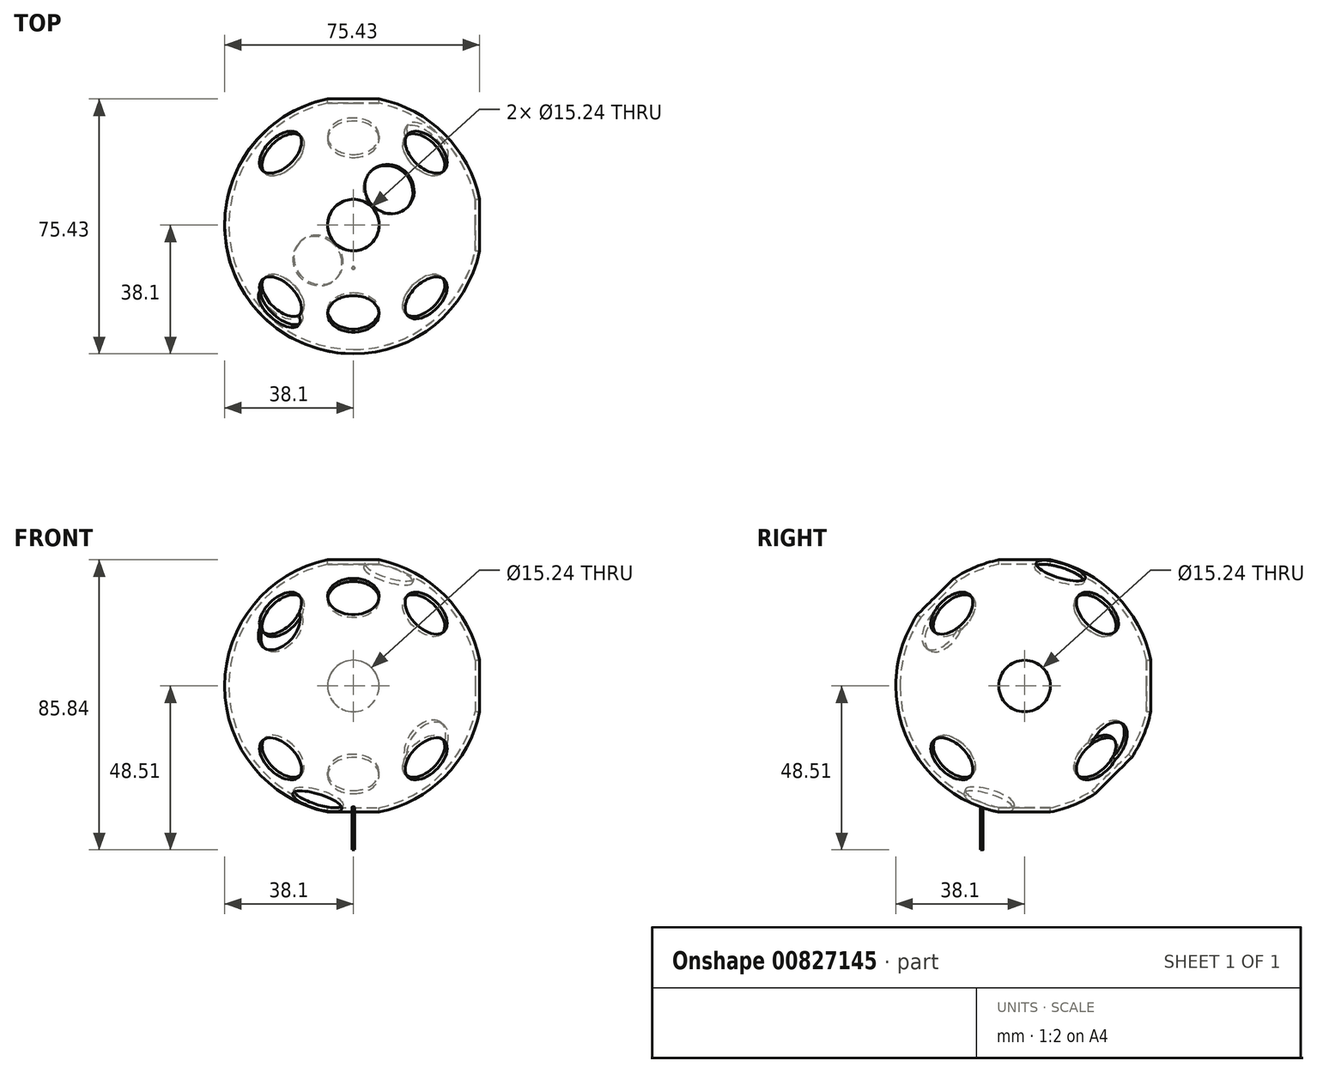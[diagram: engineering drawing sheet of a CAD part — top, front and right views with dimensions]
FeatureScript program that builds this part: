
annotation { "Feature Type Name" : "Feature", "Feature Type Description" : "" }
export const myFeature = defineFeature(function(context is Context, id is Id, definition is map)
    precondition{}
    {
        {
            assignVariable(context, id + "F0", {"name" : "SphereDiameter", "anyValue" : 3});
        }
        {
            var Q0;
            Q0=qCreatedBy(makeId("Top.planeOp"),FACE);
            var sketch = newSketch(context, id + "F1", { "sketchPlane" : qUnion([Q0])});
            skArc(sketch, "E0", {"start": v(0, 38.1) * mm, "mid": v(-38.1, 0) * mm, "end": v(0, -38.1) * mm});
            skLineSegment(sketch, "E1", {"start": v(0, 38.1) * mm, "end": v(0, -38.1) * mm});
            skSolve(sketch);
        }
        {
            var Q0;
            Q0=qSketchRegion(id+"F1",true);
            var Q1;
            Q1=sQuery(id+"F1.wireOp",EDGE,"E1");
            revolve(context, id + "F2", {"surfaceOperationType" : NewSurfaceOperationType.NEW, "entities" : qUnion([Q0]), "axis" : qUnion([Q1]), "revolveType" : RevolveType.FULL});
        }
        {
            var Q0;
            Q0=qCreatedBy(makeId("Top.planeOp"),FACE);
            var sketch = newSketch(context, id + "F3", { "sketchPlane" : qUnion([Q0])});
            skLineSegment(sketch, "E2", {"start": v(0, 0) * mm, "end": v(0, 38.1) * mm});
            skLineSegment(sketch, "E3", {"start": v(0, 0) * mm, "end": v(0, -38.1) * mm});
            skLineSegment(sketch, "E4", {"start": v(0, 0) * mm, "end": v(38.1, 0) * mm});
            skLineSegment(sketch, "E5", {"start": v(0, 0) * mm, "end": v(-38.1, 0) * mm});
            skSolve(sketch);
        }
        {
            var Q0;
            Q0=qCreatedBy(makeId("Front.planeOp"),FACE);
            var sketch = newSketch(context, id + "F4", { "sketchPlane" : qUnion([Q0])});
            skLineSegment(sketch, "E6", {"start": v(0, 0) * mm, "end": v(0, 38.1) * mm});
            skLineSegment(sketch, "E7", {"start": v(0, 0) * mm, "end": v(0, -38.1) * mm});
            skSolve(sketch);
        }
        {
            var Q0;
            Q0=sQuery(id+"F4.wireOp",VERTEX,"E6.end");
            var Q1;
            Q1=sQuery(id+"F3.wireOp",VERTEX,"E3.end");
            var Q2;
            Q2=sQuery(id+"F3.wireOp",VERTEX,"E4.end");
            cPlane(context, id + "F5", {"entities" : qUnion([Q0, Q1, Q2]), "cplaneType" : CPlaneType.THREE_POINT, "offset" : 25.4 * mm, "width" : 152.4 * mm, "height" : 152.4 * mm});
        }
        {
            var Q0;
            Q0=qCreatedBy(id+"F5.planeOp",FACE);
            var sketch = newSketch(context, id + "F6", { "sketchPlane" : qUnion([Q0])});
            skLineSegment(sketch, "E8", {"start": v(-31.1, 0) * mm, "end": v(15.55, -26.94) * mm});
            skLineSegment(sketch, "E9", {"start": v(15.55, -26.94) * mm, "end": v(15.55, 26.94) * mm});
            skLineSegment(sketch, "E10", {"start": v(15.55, 26.94) * mm, "end": v(-31.1, 0) * mm});
            skLineSegment(sketch, "E11", {"start": v(15.55, 26.94) * mm, "end": v(0, 0) * mm});
            skSolve(sketch);
        }
        {
            var Q0;
            Q0=sQuery(id+"F4.wireOp",VERTEX,"E6.end");
            var Q1;
            Q1=sQuery(id+"F6.wireOp",VERTEX,"E11.end");
            var Q2;
            Q2=sQuery(id+"F3.wireOp",VERTEX,"E3.start");
            cPlane(context, id + "F7", {"entities" : qUnion([Q0, Q1, Q2]), "cplaneType" : CPlaneType.THREE_POINT, "offset" : 25.4 * mm, "width" : 152.4 * mm, "height" : 152.4 * mm});
        }
        {
            var Q0;
            Q0=qCreatedBy(id+"F7.planeOp",FACE);
            var sketch = newSketch(context, id + "F8", { "sketchPlane" : qUnion([Q0])});
            skLineSegment(sketch, "E12", {"start": v(0, 0) * mm, "end": v(17.96, 12.7) * mm});
            skLineSegment(sketch, "E13", {"start": v(10.37, 7.33) * mm, "end": v(17.96, 12.7) * mm});
            skLineSegment(sketch, "E14", {"start": v(0, 0) * mm, "end": v(-10.37, -7.33) * mm});
            skSolve(sketch);
        }
        {
            var Q0;
            Q0=sQuery(id+"F3.wireOp",VERTEX,"E2.end");
            var Q1;
            Q1=sQuery(id+"F4.wireOp",VERTEX,"E6.end");
            var Q2;
            Q2=sQuery(id+"F3.wireOp",VERTEX,"E5.end");
            cPlane(context, id + "F9", {"entities" : qUnion([Q0, Q1, Q2]), "cplaneType" : CPlaneType.THREE_POINT, "offset" : 25.4 * mm, "width" : 152.4 * mm, "height" : 152.4 * mm});
        }
        {
            var Q0;
            Q0=qCreatedBy(id+"F9.planeOp",FACE);
            var sketch = newSketch(context, id + "F10", { "sketchPlane" : qUnion([Q0])});
            skLineSegment(sketch, "E15", {"start": v(31.1, 0) * mm, "end": v(-15.55, 26.94) * mm});
            skLineSegment(sketch, "E16", {"start": v(-15.55, 26.94) * mm, "end": v(-15.55, -26.94) * mm});
            skLineSegment(sketch, "E17", {"start": v(-15.55, -26.94) * mm, "end": v(31.1, 0) * mm});
            skLineSegment(sketch, "E18", {"start": v(-15.55, 26.94) * mm, "end": v(0, 0) * mm});
            skSolve(sketch);
        }
        {
            var Q0;
            Q0=sQuery(id+"F4.wireOp",VERTEX,"E6.end");
            var Q1;
            Q1=qCreatedBy(makeId("Origin.pointOp"),VERTEX);
            var Q2;
            Q2=sQuery(id+"F10.wireOp",VERTEX,"E18.end");
            cPlane(context, id + "F11", {"entities" : qUnion([Q0, Q1, Q2]), "cplaneType" : CPlaneType.THREE_POINT, "offset" : 25.4 * mm, "width" : 152.4 * mm, "height" : 152.4 * mm});
        }
        {
            var Q0;
            Q0=qCreatedBy(id+"F11.planeOp",FACE);
            var sketch = newSketch(context, id + "F12", { "sketchPlane" : qUnion([Q0])});
            skLineSegment(sketch, "E19", {"start": v(0, 0) * mm, "end": v(-17.96, 12.7) * mm});
            skLineSegment(sketch, "E20", {"start": v(-17.96, 12.7) * mm, "end": v(-10.37, 7.33) * mm});
            skLineSegment(sketch, "E21", {"start": v(10.37, -7.33) * mm, "end": v(0, 0) * mm});
            skSolve(sketch);
        }
        {
            var Q0;
            Q0=sQuery(id+"F3.wireOp",VERTEX,"E2.end");
            var Q1;
            Q1=sQuery(id+"F4.wireOp",VERTEX,"E7.end");
            var Q2;
            Q2=sQuery(id+"F3.wireOp",VERTEX,"E4.end");
            cPlane(context, id + "F13", {"entities" : qUnion([Q0, Q1, Q2]), "cplaneType" : CPlaneType.THREE_POINT, "offset" : 25.4 * mm, "width" : 152.4 * mm, "height" : 152.4 * mm});
        }
        {
            var Q0;
            Q0=qCreatedBy(id+"F13.planeOp",FACE);
            var sketch = newSketch(context, id + "F14", { "sketchPlane" : qUnion([Q0])});
            skLineSegment(sketch, "E22", {"start": v(15.55, -26.94) * mm, "end": v(15.55, 26.94) * mm});
            skLineSegment(sketch, "E23", {"start": v(15.55, 26.94) * mm, "end": v(-31.1, 0) * mm});
            skLineSegment(sketch, "E24", {"start": v(-31.1, 0) * mm, "end": v(15.55, -26.94) * mm});
            skLineSegment(sketch, "E25", {"start": v(15.55, 26.94) * mm, "end": v(0, 0) * mm});
            skSolve(sketch);
        }
        {
            var Q0;
            Q0=sQuery(id+"F3.wireOp",VERTEX,"E3.start");
            var Q1;
            Q1=sQuery(id+"F3.wireOp",VERTEX,"E2.end");
            var Q2;
            Q2=sQuery(id+"F14.wireOp",VERTEX,"E25.end");
            cPlane(context, id + "F15", {"entities" : qUnion([Q0, Q1, Q2]), "cplaneType" : CPlaneType.THREE_POINT, "offset" : 25.4 * mm, "width" : 152.4 * mm, "height" : 152.4 * mm});
        }
        {
            var Q0;
            Q0=qCreatedBy(id+"F15.planeOp",FACE);
            var sketch = newSketch(context, id + "F16", { "sketchPlane" : qUnion([Q0])});
            skLineSegment(sketch, "E26", {"start": v(0, 0) * mm, "end": v(17.96, 12.7) * mm});
            skLineSegment(sketch, "E27", {"start": v(10.37, 7.33) * mm, "end": v(17.96, 12.7) * mm});
            skLineSegment(sketch, "E28", {"start": v(0, 0) * mm, "end": v(-10.37, -7.33) * mm});
            skSolve(sketch);
        }
        {
            var Q0;
            Q0=sQuery(id+"F4.wireOp",VERTEX,"E6.end");
            var Q1;
            Q1=sQuery(id+"F3.wireOp",VERTEX,"E4.end");
            var Q2;
            Q2=sQuery(id+"F3.wireOp",VERTEX,"E2.end");
            cPlane(context, id + "F17", {"entities" : qUnion([Q0, Q1, Q2]), "cplaneType" : CPlaneType.THREE_POINT, "offset" : 25.4 * mm, "width" : 152.4 * mm, "height" : 152.4 * mm});
        }
        {
            var Q0;
            Q0=qCreatedBy(id+"F17.planeOp",FACE);
            var sketch = newSketch(context, id + "F18", { "sketchPlane" : qUnion([Q0])});
            skLineSegment(sketch, "E29", {"start": v(-15.55, 26.94) * mm, "end": v(31.1, 0) * mm});
            skLineSegment(sketch, "E30", {"start": v(31.1, 0) * mm, "end": v(-15.55, -26.94) * mm});
            skLineSegment(sketch, "E31", {"start": v(-15.55, -26.94) * mm, "end": v(-15.55, 26.94) * mm});
            skLineSegment(sketch, "E32", {"start": v(-15.55, 26.94) * mm, "end": v(0, 0) * mm});
            skSolve(sketch);
        }
        {
            var Q0;
            Q0=sQuery(id+"F4.wireOp",VERTEX,"E6.end");
            var Q1;
            Q1=sQuery(id+"F18.wireOp",VERTEX,"E32.end");
            var Q2;
            Q2=sQuery(id+"F3.wireOp",VERTEX,"E3.start");
            cPlane(context, id + "F19", {"entities" : qUnion([Q0, Q1, Q2]), "cplaneType" : CPlaneType.THREE_POINT, "offset" : 25.4 * mm, "width" : 152.4 * mm, "height" : 152.4 * mm});
        }
        {
            var Q0;
            Q0=qCreatedBy(id+"F19.planeOp",FACE);
            var sketch = newSketch(context, id + "F20", { "sketchPlane" : qUnion([Q0])});
            skLineSegment(sketch, "E33", {"start": v(0, 0) * mm, "end": v(17.96, 12.7) * mm});
            skLineSegment(sketch, "E34", {"start": v(10.37, 7.33) * mm, "end": v(17.96, 12.7) * mm});
            skLineSegment(sketch, "E35", {"start": v(0, 0) * mm, "end": v(-10.37, -7.33) * mm});
            skSolve(sketch);
        }
        {
            var Q0;
            Q0=qCreatedBy(makeId("Top.planeOp"),FACE);
            var Q1;
            Q1=sQuery(id+"F4.wireOp",VERTEX,"E6.end");
            cPlane(context, id + "F21", {"entities" : qUnion([Q0, Q1]), "cplaneType" : CPlaneType.PLANE_POINT, "offset" : 25.4 * mm, "width" : 152.4 * mm, "height" : 152.4 * mm});
        }
        {
            var Q0;
            Q0=qCreatedBy(id+"F21.planeOp",FACE);
            var sketch = newSketch(context, id + "F22", { "sketchPlane" : qUnion([Q0])});
            skCircle(sketch, "E36", {"center": v(0, 0) * mm, "radius": 7.62 * mm});
            skSolve(sketch);
        }
        {
            var Q0;
            Q0=qSketchRegion(id+"F22",true);
            extrude(context, id + "F23", {"entities" : qUnion([Q0]), "operationType" : NewBodyOperationType.REMOVE, "endBound" : BoundingType.SYMMETRIC, "oppositeDirection" : true, "depth" : 76.2 * mm, "offsetDistance" : 25.4 * mm});
        }
        {
            var Q0;
            Q0=qCreatedBy(makeId("Right.planeOp"),FACE);
            var Q1;
            Q1=sQuery(id+"F3.wireOp",VERTEX,"E4.end");
            cPlane(context, id + "F24", {"entities" : qUnion([Q0, Q1]), "cplaneType" : CPlaneType.PLANE_POINT, "offset" : 25.4 * mm, "width" : 152.4 * mm, "height" : 152.4 * mm});
        }
        {
            var Q0;
            Q0=qCreatedBy(id+"F24.planeOp",FACE);
            var sketch = newSketch(context, id + "F25", { "sketchPlane" : qUnion([Q0])});
            skCircle(sketch, "E37", {"center": v(0, 0) * mm, "radius": 7.62 * mm});
            skSolve(sketch);
        }
        {
            var Q0;
            Q0=qSketchRegion(id+"F25",true);
            extrude(context, id + "F26", {"entities" : qUnion([Q0]), "operationType" : NewBodyOperationType.REMOVE, "endBound" : BoundingType.SYMMETRIC, "oppositeDirection" : true, "depth" : 76.2 * mm, "offsetDistance" : 25.4 * mm});
        }
        {
            var Q0;
            Q0=qCreatedBy(makeId("Front.planeOp"),FACE);
            var Q1;
            Q1=sQuery(id+"F3.wireOp",VERTEX,"E2.end");
            cPlane(context, id + "F27", {"entities" : qUnion([Q0, Q1]), "cplaneType" : CPlaneType.PLANE_POINT, "offset" : 25.4 * mm, "width" : 152.4 * mm, "height" : 152.4 * mm});
        }
        {
            var Q0;
            Q0=qCreatedBy(id+"F27.planeOp",FACE);
            var sketch = newSketch(context, id + "F28", { "sketchPlane" : qUnion([Q0])});
            skCircle(sketch, "E38", {"center": v(0, 0) * mm, "radius": 7.62 * mm});
            skSolve(sketch);
        }
        {
            var Q0;
            Q0=qSketchRegion(id+"F28",true);
            extrude(context, id + "F29", {"entities" : qUnion([Q0]), "operationType" : NewBodyOperationType.REMOVE, "endBound" : BoundingType.SYMMETRIC, "depth" : 76.2 * mm, "offsetDistance" : 25.4 * mm});
        }
        {
            var Q0;
            Q0=qCreatedBy(id+"F5.planeOp",FACE);
            var Q1;
            Q1=sQuery(id+"F8.wireOp",VERTEX,"E13.end");
            cPlane(context, id + "F30", {"entities" : qUnion([Q0, Q1]), "cplaneType" : CPlaneType.PLANE_POINT, "offset" : 25.4 * mm, "width" : 152.4 * mm, "height" : 152.4 * mm});
        }
        {
            var Q0;
            Q0=qCreatedBy(id+"F30.planeOp",FACE);
            var sketch = newSketch(context, id + "F31", { "sketchPlane" : qUnion([Q0])});
            skCircle(sketch, "E39", {"center": v(0, 0) * mm, "radius": 7.62 * mm});
            skSolve(sketch);
        }
        {
            var Q0;
            Q0=qSketchRegion(id+"F31",true);
            extrude(context, id + "F32", {"entities" : qUnion([Q0]), "operationType" : NewBodyOperationType.REMOVE, "endBound" : BoundingType.SYMMETRIC, "depth" : 254 * mm, "offsetDistance" : 25.4 * mm});
        }
        {
            var Q0;
            Q0=qCreatedBy(id+"F9.planeOp",FACE);
            var Q1;
            Q1=sQuery(id+"F12.wireOp",VERTEX,"E20.start");
            cPlane(context, id + "F33", {"entities" : qUnion([Q0, Q1]), "cplaneType" : CPlaneType.PLANE_POINT, "offset" : 25.4 * mm, "width" : 152.4 * mm, "height" : 152.4 * mm});
        }
        {
            var Q0;
            Q0=qCreatedBy(id+"F33.planeOp",FACE);
            var sketch = newSketch(context, id + "F34", { "sketchPlane" : qUnion([Q0])});
            skCircle(sketch, "E40", {"center": v(0, 0) * mm, "radius": 7.62 * mm});
            skSolve(sketch);
        }
        {
            var Q0;
            Q0=qSketchRegion(id+"F34",true);
            extrude(context, id + "F35", {"entities" : qUnion([Q0]), "operationType" : NewBodyOperationType.REMOVE, "endBound" : BoundingType.SYMMETRIC, "depth" : 254 * mm, "offsetDistance" : 25.4 * mm});
        }
        {
            var Q0;
            Q0=qCreatedBy(id+"F17.planeOp",FACE);
            var Q1;
            Q1=sQuery(id+"F20.wireOp",VERTEX,"E34.end");
            cPlane(context, id + "F36", {"entities" : qUnion([Q0, Q1]), "cplaneType" : CPlaneType.PLANE_POINT, "offset" : 25.4 * mm, "width" : 152.4 * mm, "height" : 152.4 * mm});
        }
        {
            var Q0;
            Q0=qCreatedBy(id+"F36.planeOp",FACE);
            var sketch = newSketch(context, id + "F37", { "sketchPlane" : qUnion([Q0])});
            skCircle(sketch, "E41", {"center": v(0, 0) * mm, "radius": 7.62 * mm});
            skSolve(sketch);
        }
        {
            var Q0;
            Q0=qSketchRegion(id+"F37",true);
            extrude(context, id + "F38", {"entities" : qUnion([Q0]), "operationType" : NewBodyOperationType.REMOVE, "endBound" : BoundingType.SYMMETRIC, "depth" : 254 * mm, "offsetDistance" : 25.4 * mm});
        }
        {
            var Q0;
            Q0=qCreatedBy(id+"F13.planeOp",FACE);
            var Q1;
            Q1=sQuery(id+"F16.wireOp",VERTEX,"E27.end");
            cPlane(context, id + "F39", {"entities" : qUnion([Q0, Q1]), "cplaneType" : CPlaneType.PLANE_POINT, "offset" : 25.4 * mm, "width" : 152.4 * mm, "height" : 152.4 * mm});
        }
        {
            var Q0;
            Q0=qCreatedBy(id+"F39.planeOp",FACE);
            var sketch = newSketch(context, id + "F40", { "sketchPlane" : qUnion([Q0])});
            skCircle(sketch, "E42", {"center": v(0, 0) * mm, "radius": 7.62 * mm});
            skSolve(sketch);
        }
        {
            var Q0;
            Q0=qSketchRegion(id+"F40",true);
            extrude(context, id + "F41", {"entities" : qUnion([Q0]), "operationType" : NewBodyOperationType.REMOVE, "endBound" : BoundingType.SYMMETRIC, "depth" : 254 * mm, "offsetDistance" : 25.4 * mm});
        }
        {
            var Q0;
            Q0=qCreatedBy(makeId("Top.planeOp"),FACE);
            var sketch = newSketch(context, id + "F42", { "sketchPlane" : qUnion([Q0])});
            skArc(sketch, "E43", {"start": v(0, 36.83) * mm, "mid": v(-36.83, 0) * mm, "end": v(0, -36.83) * mm});
            skLineSegment(sketch, "E44", {"start": v(0, 36.83) * mm, "end": v(0, -36.83) * mm});
            skSolve(sketch);
        }
        {
            var Q0;
            Q0=qSketchRegion(id+"F42",true);
            var Q1;
            Q1=sQuery(id+"F3.wireOp",EDGE,"E2");
            revolve(context, id + "F43", {"operationType" : NewBodyOperationType.REMOVE, "surfaceOperationType" : NewSurfaceOperationType.NEW, "entities" : qUnion([Q0]), "axis" : qUnion([Q1]), "revolveType" : RevolveType.FULL, "oppositeDirection" : true});
        }
        {
            var Q0;
            Q0=sQuery(id+"F12.wireOp",VERTEX,"E20.start");
            var Q1;
            Q1=sQuery(id+"F28.wireOp",VERTEX,"E38.center");
            var Q2;
            Q2=sQuery(id+"F20.wireOp",VERTEX,"E34.end");
            cPlane(context, id + "F44", {"entities" : qUnion([Q0, Q1, Q2]), "cplaneType" : CPlaneType.THREE_POINT, "offset" : 25.4 * mm, "width" : 152.4 * mm, "height" : 152.4 * mm});
        }
        {
            var Q0;
            Q0=qCreatedBy(id+"F44.planeOp",FACE);
            var sketch = newSketch(context, id + "F45", { "sketchPlane" : qUnion([Q0])});
            skLineSegment(sketch, "E45", {"start": v(7.33, 5.43) * mm, "end": v(-7.33, 5.43) * mm});
            skLineSegment(sketch, "E46", {"start": v(0, 37.06) * mm, "end": v(0, 5.43) * mm});
            skSolve(sketch);
        }
        {
            var Q0;
            Q0=sQuery(id+"F4.wireOp",VERTEX,"E6.end");
            var Q1;
            Q1=sQuery(id+"F20.wireOp",VERTEX,"E34.end");
            var Q2;
            Q2=sQuery(id+"F12.wireOp",VERTEX,"E20.start");
            cPlane(context, id + "F46", {"entities" : qUnion([Q0, Q1, Q2]), "cplaneType" : CPlaneType.THREE_POINT, "offset" : 25.4 * mm, "width" : 152.4 * mm, "height" : 152.4 * mm});
        }
        {
            var Q0;
            Q0=qCreatedBy(id+"F46.planeOp",FACE);
            var sketch = newSketch(context, id + "F47", { "sketchPlane" : qUnion([Q0])});
            skLineSegment(sketch, "E47", {"start": v(0, 37.06) * mm, "end": v(0, 5.43) * mm});
            skSolve(sketch);
        }
        {
            var Q0;
            Q0=qCreatedBy(id+"F46.planeOp",FACE);
            var sketch = newSketch(context, id + "F48", { "sketchPlane" : qUnion([Q0])});
            skLineSegment(sketch, "E48", {"start": v(0, -2.1) * mm, "end": v(0, 5.43) * mm});
            skSolve(sketch);
        }
        {
            var Q0;
            Q0=qCreatedBy(id+"F44.planeOp",FACE);
            var sketch = newSketch(context, id + "F49", { "sketchPlane" : qUnion([Q0])});
            skLineSegment(sketch, "E49", {"start": v(0, 5.43) * mm, "end": v(0, -2.1) * mm});
            skSolve(sketch);
        }
        {
            var Q0;
            Q0=sQuery(id+"F12.wireOp",VERTEX,"E19.start");
            var Q1;
            Q1=sQuery(id+"F12.wireOp",VERTEX,"E20.start");
            var Q2;
            Q2=sQuery(id+"F20.wireOp",VERTEX,"E34.end");
            cPlane(context, id + "F50", {"entities" : qUnion([Q0, Q1, Q2]), "cplaneType" : CPlaneType.THREE_POINT, "offset" : 25.4 * mm, "width" : 152.4 * mm, "height" : 152.4 * mm});
        }
        {
            var Q0;
            Q0=sQuery(id+"F49.wireOp",VERTEX,"E49.start");
            var Q1;
            Q1=sQuery(id+"F48.wireOp",VERTEX,"E48.start");
            var Q2;
            Q2=sQuery(id+"F48.wireOp",VERTEX,"E48.end");
            cPlane(context, id + "F51", {"entities" : qUnion([Q0, Q1, Q2]), "cplaneType" : CPlaneType.THREE_POINT, "offset" : 25.4 * mm, "width" : 152.4 * mm, "height" : 152.4 * mm});
        }
        {
            var Q0;
            Q0=qCreatedBy(id+"F51.planeOp",FACE);
            var sketch = newSketch(context, id + "F52", { "sketchPlane" : qUnion([Q0])});
            skLineSegment(sketch, "E50", {"start": v(1.61, 15.15) * mm, "end": v(15.53, 1.33) * mm});
            skSolve(sketch);
        }
        {
            var Q0;
            Q0=sQuery(id+"F52.wireOp",EDGE,"E50");
            var Q1;
            Q1=qCreatedBy(id+"F44.planeOp",FACE);
            cPlane(context, id + "F53", {"entities" : qUnion([Q0, Q1]), "cplaneType" : CPlaneType.LINE_ANGLE, "offset" : 25.4 * mm, "angle" : 0 * degree, "width" : 152.4 * mm, "height" : 152.4 * mm});
        }
        {
            var Q0;
            Q0=qCreatedBy(id+"F53.planeOp",FACE);
            var sketch = newSketch(context, id + "F54", { "sketchPlane" : qUnion([Q0])});
            skCircle(sketch, "E51", {"center": v(0, 0) * mm, "radius": 7.62 * mm});
            skSolve(sketch);
        }
        {
            var Q0;
            Q0=qSketchRegion(id+"F54",true);
            extrude(context, id + "F55", {"entities" : qUnion([Q0]), "operationType" : NewBodyOperationType.REMOVE, "endBound" : BoundingType.SYMMETRIC, "depth" : 127 * mm, "offsetDistance" : 25.4 * mm});
        }
        {
            var Q0;
            Q0=sQuery(id+"F8.wireOp",VERTEX,"E13.end");
            var Q1;
            Q1=qCreatedBy(makeId("Origin.pointOp"),VERTEX);
            var Q2;
            Q2=sQuery(id+"F20.wireOp",VERTEX,"E34.end");
            cPlane(context, id + "F56", {"entities" : qUnion([Q0, Q1, Q2]), "cplaneType" : CPlaneType.THREE_POINT, "offset" : 25.4 * mm, "width" : 152.4 * mm, "height" : 152.4 * mm});
        }
        {
            var Q0;
            Q0=qCreatedBy(id+"F56.planeOp",FACE);
            var sketch = newSketch(context, id + "F57", { "sketchPlane" : qUnion([Q0])});
            skLineSegment(sketch, "E52", {"start": v(10.37, 7.33) * mm, "end": v(10.37, -7.33) * mm});
            skLineSegment(sketch, "E53", {"start": v(0, 0) * mm, "end": v(10.37, 0) * mm});
            skSolve(sketch);
        }
        {
            var Q0;
            Q0=sQuery(id+"F57.wireOp",VERTEX,"E53.end");
            var Q1;
            Q1=sQuery(id+"F4.wireOp",VERTEX,"E6.end");
            var Q2;
            Q2=sQuery(id+"F8.wireOp",VERTEX,"E12.start");
            cPlane(context, id + "F58", {"entities" : qUnion([Q0, Q1, Q2]), "cplaneType" : CPlaneType.THREE_POINT, "offset" : 25.4 * mm, "width" : 152.4 * mm, "height" : 152.4 * mm});
        }
        {
            var Q0;
            Q0=qCreatedBy(id+"F58.planeOp",FACE);
            var sketch = newSketch(context, id + "F59", { "sketchPlane" : qUnion([Q0])});
            skLineSegment(sketch, "E54", {"start": v(-7.33, 7.33) * mm, "end": v(0, 38.1) * mm});
            skLineSegment(sketch, "E55", {"start": v(-7.33, 7.33) * mm, "end": v(-38.1, 0) * mm});
            skLineSegment(sketch, "E56", {"start": v(0, 14.66) * mm, "end": v(-14.66, 0) * mm});
            skSolve(sketch);
        }
        {
            var Q0;
            Q0=sQuery(id+"F57.wireOp",VERTEX,"E53.end");
            var Q1;
            Q1=sQuery(id+"F59.wireOp",VERTEX,"E56.start");
            var Q2;
            Q2=sQuery(id+"F8.wireOp",VERTEX,"E13.end");
            cPlane(context, id + "F60", {"entities" : qUnion([Q0, Q1, Q2]), "cplaneType" : CPlaneType.THREE_POINT, "offset" : 25.4 * mm, "width" : 152.4 * mm, "height" : 152.4 * mm});
        }
        {
            var Q0;
            Q0=qCreatedBy(id+"F60.planeOp",FACE);
            var sketch = newSketch(context, id + "F61", { "sketchPlane" : qUnion([Q0])});
            skCircle(sketch, "E57", {"center": v(0, 0) * mm, "radius": 7.62 * mm});
            skSolve(sketch);
        }
        {
            var Q0;
            Q0=qSketchRegion(id+"F61",true);
            extrude(context, id + "F62", {"entities" : qUnion([Q0]), "operationType" : NewBodyOperationType.REMOVE, "endBound" : BoundingType.SYMMETRIC, "depth" : 127 * mm, "offsetDistance" : 25.4 * mm});
        }
        {
            var Q0;
            Q0=sQuery(id+"F3.wireOp",VERTEX,"E5.end");
            var Q1;
            Q1=qCreatedBy(makeId("Origin.pointOp"),VERTEX);
            var Q2;
            Q2=sQuery(id+"F3.wireOp",VERTEX,"E3.end");
            cPlane(context, id + "F63", {"entities" : qUnion([Q0, Q1, Q2]), "cplaneType" : CPlaneType.THREE_POINT, "offset" : 25.4 * mm, "width" : 152.4 * mm, "height" : 152.4 * mm});
        }
        {
            var Q0;
            Q0=qCreatedBy(id+"F63.planeOp",FACE);
            var sketch = newSketch(context, id + "F64", { "sketchPlane" : qUnion([Q0])});
            skLineSegment(sketch, "E58", {"start": v(0, -38.1) * mm, "end": v(-38.1, 0) * mm});
            skLineSegment(sketch, "E59", {"start": v(0, 0) * mm, "end": v(-19.05, -19.05) * mm});
            skSolve(sketch);
        }
        {
            var Q0;
            Q0=sQuery(id+"F16.wireOp",VERTEX,"E28.end");
            var Q1;
            Q1=sQuery(id+"F20.wireOp",VERTEX,"E35.end");
            var Q2;
            Q2=sQuery(id+"F57.wireOp",VERTEX,"E53.start");
            cPlane(context, id + "F65", {"entities" : qUnion([Q0, Q1, Q2]), "cplaneType" : CPlaneType.THREE_POINT, "offset" : 25.4 * mm, "width" : 152.4 * mm, "height" : 152.4 * mm});
        }
        {
            var Q0;
            Q0=qCreatedBy(id+"F65.planeOp",FACE);
            var sketch = newSketch(context, id + "F66", { "sketchPlane" : qUnion([Q0])});
            skLineSegment(sketch, "E60", {"start": v(10.37, -7.33) * mm, "end": v(10.37, 7.33) * mm});
            skLineSegment(sketch, "E61", {"start": v(10.37, 0) * mm, "end": v(26.94, 0) * mm});
            skPoint(sketch, "E61.endSnap0", {"position": v(10.37, 0) * mm});
            skSolve(sketch);
        }
        {
            var Q0;
            Q0=qCreatedBy(id+"F63.planeOp",FACE);
            var sketch = newSketch(context, id + "F67", { "sketchPlane" : qUnion([Q0])});
            skLineSegment(sketch, "E62", {"start": v(-14.66, 0) * mm, "end": v(0, -14.66) * mm});
            skLineSegment(sketch, "E63", {"start": v(-14.66, 0) * mm, "end": v(-38.1, 0) * mm});
            skLineSegment(sketch, "E64", {"start": v(-14.66, 0) * mm, "end": v(-14.66, 0) * mm});
            skLineSegment(sketch, "E65", {"start": v(0, -14.66) * mm, "end": v(0, -38.1) * mm});
            skSolve(sketch);
        }
        {
            var Q0;
            Q0=sQuery(id+"F67.wireOp",VERTEX,"E63.end");
            var Q1;
            Q1=sQuery(id+"F67.wireOp",VERTEX,"E65.end");
            var Q2;
            Q2=sQuery(id+"F20.wireOp",VERTEX,"E35.end");
            cPlane(context, id + "F68", {"entities" : qUnion([Q0, Q1, Q2]), "cplaneType" : CPlaneType.THREE_POINT, "offset" : 25.4 * mm, "width" : 152.4 * mm, "height" : 152.4 * mm});
        }
        {
            var Q0;
            Q0=qCreatedBy(id+"F68.planeOp",FACE);
            var sketch = newSketch(context, id + "F69", { "sketchPlane" : qUnion([Q0])});
            skCircle(sketch, "E66", {"center": v(0, 0) * mm, "radius": 7.62 * mm});
            skSolve(sketch);
        }
        {
            var Q0;
            Q0=qSketchRegion(id+"F69",true);
            extrude(context, id + "F70", {"entities" : qUnion([Q0]), "operationType" : NewBodyOperationType.REMOVE, "endBound" : BoundingType.SYMMETRIC, "oppositeDirection" : true, "depth" : 101.6 * mm, "offsetDistance" : 25.4 * mm});
        }
        {
            var Q0;
            Q0=qCreatedBy(makeId("Top.planeOp"),FACE);
            cPlane(context, id + "F71", {"entities" : qUnion([Q0]), "cplaneType" : CPlaneType.OFFSET, "offset" : ((getVariable(context, 'SphereDiameter') / 2) - (getVariable(context, 'SphereDiameter') / 90)) * mm, "oppositeDirection" : true, "width" : 152.4 * mm, "height" : 152.4 * mm});
        }
        {
            var Q0;
            Q0=qCreatedBy(id+"F71.planeOp",FACE);
            var sketch = newSketch(context, id + "F72", { "sketchPlane" : qUnion([Q0])});
            skCircle(sketch, "E67", {"center": v(0, 0) * mm, "radius": 7.62 * mm});
            skCircle(sketch, "E68", {"center": v(0, 0) * mm, "radius": 2.86 * mm});
            skSolve(sketch);
        }
        {
            var Q0;
            Q0=qCreatedBy(makeId("Top.planeOp"),FACE);
            var sketch = newSketch(context, id + "F73", { "sketchPlane" : qUnion([Q0])});
            skCircle(sketch, "E69", {"center": v(0, 0) * mm, "radius": 7.62 * mm});
            skSolve(sketch);
        }
        {
            var Q0;
            Q0=qSketchRegion(id+"F73",true);
            extrude(context, id + "F74", {"entities" : qUnion([Q0]), "operationType" : NewBodyOperationType.REMOVE, "endBound" : BoundingType.THROUGH_ALL, "oppositeDirection" : true, "depth" : (getVariable(context, 'SphereDiameter') * 3) * mm, "offsetDistance" : 25.4 * mm});
        }
        {
            var Q0;
            Q0=qCreatedBy(makeId("Top.planeOp"),FACE);
            cPlane(context, id + "F75", {"entities" : qUnion([Q0]), "cplaneType" : CPlaneType.OFFSET, "offset" : 35.56 * mm, "oppositeDirection" : true, "width" : 152.4 * mm, "height" : 152.4 * mm});
        }
        {
            var Q0;
            Q0=qCreatedBy(id+"F75.planeOp",FACE);
            var sketch = newSketch(context, id + "F76", { "sketchPlane" : qUnion([Q0])});
            skCircle(sketch, "E70", {"center": v(0, -12.7) * mm, "radius": 0.4 * mm});
            skSolve(sketch);
        }
        {
            var Q0;
            Q0 = qSketchRegion(id + "F76", true);
            extrude(context, id + "F77", {"entities" : qUnion([Q0]), "operationType" : NewBodyOperationType.ADD, "oppositeDirection" : true, "depth" : 12.95 * mm, "offsetDistance" : 25.4 * mm});
        }
        {
            var Q0;
            Q0=qCreatedBy(makeId("Front.planeOp"),FACE);
            var sketch = newSketch(context, id + "F78", { "sketchPlane" : qUnion([Q0])});
            skLineSegment(sketch, "E71", {"start": v(0, -37.84) * mm, "end": v(0, 0) * mm});
            skSolve(sketch);
        }
    });
